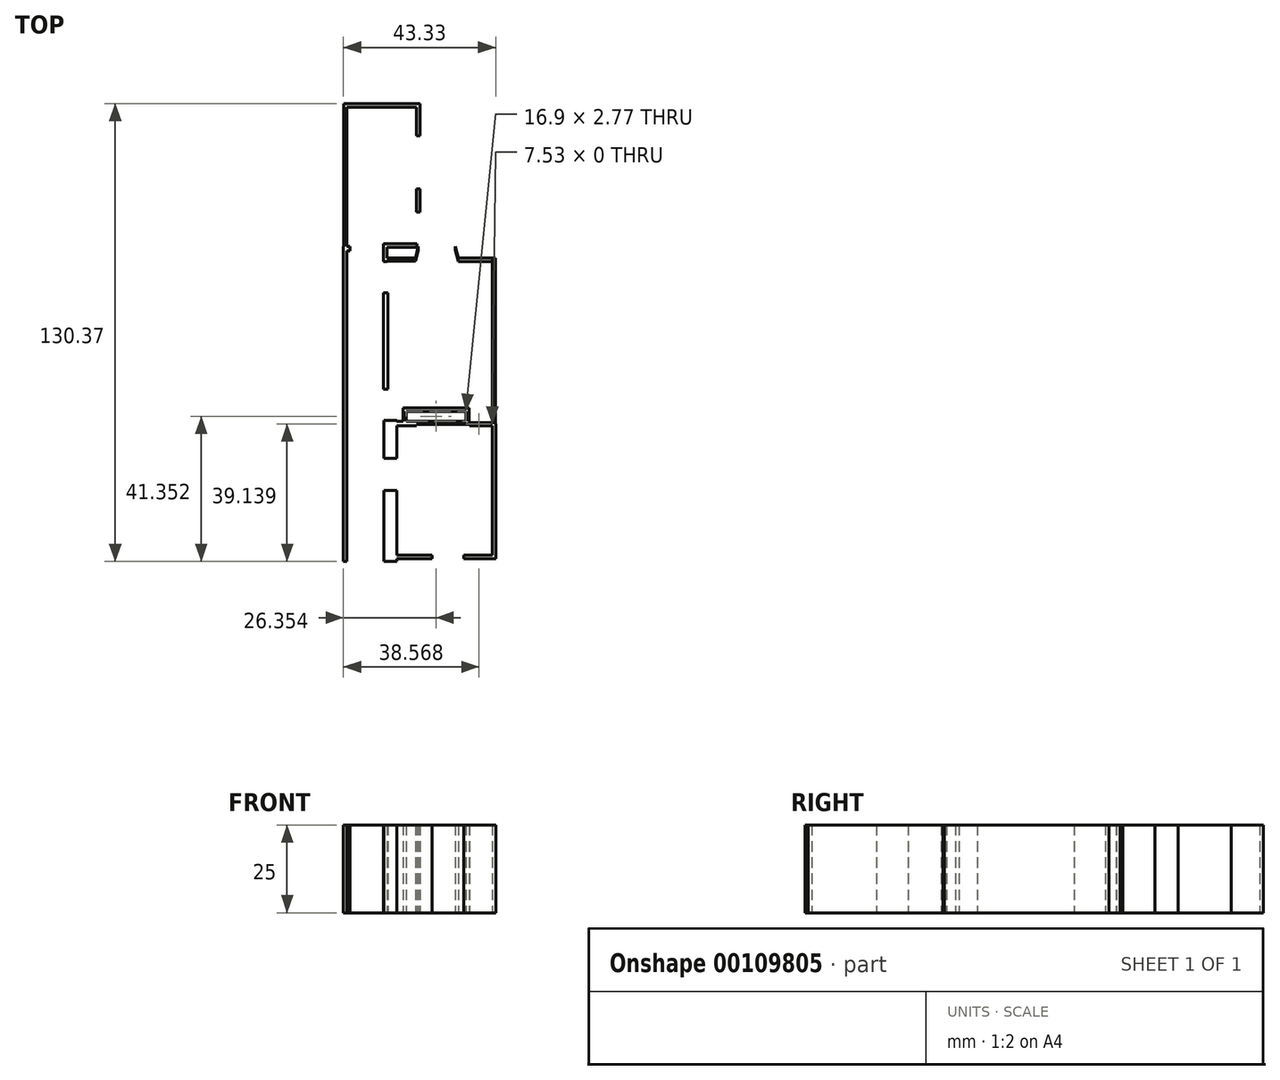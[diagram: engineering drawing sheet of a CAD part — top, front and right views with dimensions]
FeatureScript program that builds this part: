
annotation { "Feature Type Name" : "Feature", "Feature Type Description" : "" }
export const myFeature = defineFeature(function(context is Context, id is Id, definition is map)
    precondition{}
    {
        {
            var Q0;
            Q0=qCreatedBy(makeId("Top.planeOp"),FACE);
            var sketch = newSketch(context, id + "F0", { "sketchPlane" : qUnion([Q0])});
            skLineSegment(sketch, "E0.bottom", {"start": v(-26.92, 68.59) * mm, "end": v(-46.73, 68.59) * mm});
            skLineSegment(sketch, "E0.top", {"start": v(-26.92, 69.59) * mm, "end": v(-46.73, 69.59) * mm});
            skLineSegment(sketch, "E0.left", {"start": v(-26.92, 68.59) * mm, "end": v(-26.92, 69.59) * mm});
            skLineSegment(sketch, "E0.right", {"start": v(-46.73, 68.59) * mm, "end": v(-46.73, 69.59) * mm});
            skLineSegment(sketch, "E1.bottom", {"start": v(-26.94, 60.38) * mm, "end": v(-25.94, 60.38) * mm});
            skLineSegment(sketch, "E1.top", {"start": v(-26.94, 68.59) * mm, "end": v(-25.94, 68.59) * mm});
            skLineSegment(sketch, "E1.left", {"start": v(-26.94, 60.38) * mm, "end": v(-26.94, 68.59) * mm});
            skLineSegment(sketch, "E1.right", {"start": v(-25.94, 60.38) * mm, "end": v(-25.94, 68.59) * mm});
            skLineSegment(sketch, "E2.bottom", {"start": v(-46.74, 28.9) * mm, "end": v(-47.74, 28.9) * mm});
            skLineSegment(sketch, "E2.top", {"start": v(-46.74, 68.59) * mm, "end": v(-47.74, 68.59) * mm});
            skLineSegment(sketch, "E2.left", {"start": v(-46.74, 28.9) * mm, "end": v(-46.74, 68.59) * mm});
            skLineSegment(sketch, "E2.right", {"start": v(-47.74, 28.9) * mm, "end": v(-47.74, 68.59) * mm});
            skLineSegment(sketch, "E3.bottom", {"start": v(-46.74, 28.9) * mm, "end": v(-45.92, 28.9) * mm});
            skLineSegment(sketch, "E3.top", {"start": v(-46.74, 27.65) * mm, "end": v(-45.92, 27.65) * mm});
            skLineSegment(sketch, "E3.left", {"start": v(-46.74, 28.9) * mm, "end": v(-46.74, 27.65) * mm});
            skLineSegment(sketch, "E3.right", {"start": v(-45.92, 28.9) * mm, "end": v(-45.92, 27.65) * mm});
            skLineSegment(sketch, "E4.bottom", {"start": v(-36.42, 29.64) * mm, "end": v(-26.9, 29.64) * mm});
            skLineSegment(sketch, "E4.top", {"start": v(-36.42, 28.64) * mm, "end": v(-26.9, 28.64) * mm});
            skLineSegment(sketch, "E4.left", {"start": v(-36.42, 29.64) * mm, "end": v(-36.42, 28.64) * mm});
            skLineSegment(sketch, "E4.right", {"start": v(-26.9, 29.64) * mm, "end": v(-26.9, 28.64) * mm});
            skLineSegment(sketch, "E5.bottom", {"start": v(-36.42, 28.64) * mm, "end": v(-35.42, 28.64) * mm});
            skLineSegment(sketch, "E5.top", {"start": v(-36.42, 24.64) * mm, "end": v(-35.42, 24.64) * mm});
            skLineSegment(sketch, "E5.left", {"start": v(-36.42, 28.64) * mm, "end": v(-36.42, 24.64) * mm});
            skLineSegment(sketch, "E5.right", {"start": v(-35.42, 28.64) * mm, "end": v(-35.42, 24.64) * mm});
            skLineSegment(sketch, "E6.bottom", {"start": v(-27.25, 24.66) * mm, "end": v(-35.42, 24.66) * mm});
            skLineSegment(sketch, "E6.top", {"start": v(-27.25, 25.66) * mm, "end": v(-35.42, 25.66) * mm});
            skLineSegment(sketch, "E6.left", {"start": v(-27.25, 24.66) * mm, "end": v(-27.25, 25.66) * mm});
            skLineSegment(sketch, "E6.right", {"start": v(-35.42, 24.66) * mm, "end": v(-35.42, 25.66) * mm});
            skLineSegment(sketch, "E7.bottom", {"start": v(-26.49, 27.86) * mm, "end": v(-15.87, 27.86) * mm, "construction": true});
            skLineSegment(sketch, "E7.top", {"start": v(-26.49, 28.86) * mm, "end": v(-15.87, 28.86) * mm, "construction": true});
            skLineSegment(sketch, "E7.left", {"start": v(-26.49, 27.86) * mm, "end": v(-26.49, 28.86) * mm});
            skLineSegment(sketch, "E7.right", {"start": v(-15.87, 27.86) * mm, "end": v(-15.87, 28.86) * mm});
            skLineSegment(sketch, "E8", {"start": v(-26.49, 28.86) * mm, "end": v(-27.25, 25.66) * mm});
            skLineSegment(sketch, "E9", {"start": v(-27.25, 24.66) * mm, "end": v(-26.49, 27.86) * mm});
            skLineSegment(sketch, "E10.bottom", {"start": v(-5.45, 24.64) * mm, "end": v(-15.05, 24.64) * mm});
            skLineSegment(sketch, "E10.top", {"start": v(-5.45, 25.64) * mm, "end": v(-15.05, 25.64) * mm});
            skLineSegment(sketch, "E10.left", {"start": v(-5.45, 24.64) * mm, "end": v(-5.45, 25.64) * mm});
            skLineSegment(sketch, "E10.right", {"start": v(-15.05, 24.64) * mm, "end": v(-15.05, 25.64) * mm});
            skLineSegment(sketch, "E11", {"start": v(-15.87, 28.86) * mm, "end": v(-15.05, 25.64) * mm});
            skLineSegment(sketch, "E12", {"start": v(-15.87, 27.86) * mm, "end": v(-15.05, 24.64) * mm});
            skLineSegment(sketch, "E13.bottom", {"start": v(-5.44, -21.24) * mm, "end": v(-4.44, -21.24) * mm});
            skLineSegment(sketch, "E13.top", {"start": v(-5.44, 25.64) * mm, "end": v(-4.44, 25.64) * mm});
            skLineSegment(sketch, "E13.left", {"start": v(-5.44, -21.24) * mm, "end": v(-5.44, 25.64) * mm});
            skLineSegment(sketch, "E13.right", {"start": v(-4.44, -21.24) * mm, "end": v(-4.44, 25.64) * mm});
            skLineSegment(sketch, "E14.bottom", {"start": v(-36.34, 15.74) * mm, "end": v(-35.13, 15.74) * mm});
            skLineSegment(sketch, "E14.top", {"start": v(-36.34, -11.77) * mm, "end": v(-35.13, -11.77) * mm});
            skLineSegment(sketch, "E14.left", {"start": v(-36.34, 15.74) * mm, "end": v(-36.34, -11.77) * mm});
            skLineSegment(sketch, "E14.right", {"start": v(-35.13, 15.74) * mm, "end": v(-35.13, -11.77) * mm});
            skLineSegment(sketch, "E15.bottom", {"start": v(-26.92, 45.31) * mm, "end": v(-25.92, 45.31) * mm});
            skLineSegment(sketch, "E15.top", {"start": v(-26.92, 38.7) * mm, "end": v(-25.92, 38.7) * mm});
            skLineSegment(sketch, "E15.left", {"start": v(-26.92, 45.31) * mm, "end": v(-26.92, 38.7) * mm});
            skLineSegment(sketch, "E15.right", {"start": v(-25.92, 45.31) * mm, "end": v(-25.92, 38.7) * mm});
            skLineSegment(sketch, "E16.bottom", {"start": v(-46.74, 27.65) * mm, "end": v(-47.75, 27.65) * mm});
            skLineSegment(sketch, "E16.top", {"start": v(-46.74, -60.78) * mm, "end": v(-47.75, -60.78) * mm});
            skLineSegment(sketch, "E16.left", {"start": v(-46.74, 27.65) * mm, "end": v(-46.74, -60.78) * mm});
            skLineSegment(sketch, "E16.right", {"start": v(-47.75, 27.65) * mm, "end": v(-47.75, -60.78) * mm});
            skLineSegment(sketch, "E17.bottom", {"start": v(-30.85, -17.04) * mm, "end": v(-11.93, -17.04) * mm});
            skLineSegment(sketch, "E17.top", {"start": v(-30.85, -18.04) * mm, "end": v(-11.93, -18.04) * mm});
            skLineSegment(sketch, "E17.left", {"start": v(-30.85, -17.04) * mm, "end": v(-30.85, -18.04) * mm});
            skLineSegment(sketch, "E17.right", {"start": v(-11.93, -17.04) * mm, "end": v(-11.93, -18.04) * mm});
            skLineSegment(sketch, "E18.bottom", {"start": v(-30.85, -20.81) * mm, "end": v(-29.85, -20.81) * mm});
            skLineSegment(sketch, "E18.top", {"start": v(-30.85, -18.04) * mm, "end": v(-29.85, -18.04) * mm});
            skLineSegment(sketch, "E18.left", {"start": v(-30.85, -20.81) * mm, "end": v(-30.85, -18.04) * mm});
            skLineSegment(sketch, "E18.right", {"start": v(-29.85, -20.81) * mm, "end": v(-29.85, -18.04) * mm});
            skLineSegment(sketch, "E19.bottom", {"start": v(-11.94, -21.27) * mm, "end": v(-12.94, -21.27) * mm});
            skLineSegment(sketch, "E19.top", {"start": v(-11.94, -18.04) * mm, "end": v(-12.94, -18.04) * mm});
            skLineSegment(sketch, "E19.left", {"start": v(-11.94, -21.27) * mm, "end": v(-11.94, -18.04) * mm});
            skLineSegment(sketch, "E19.right", {"start": v(-12.94, -21.27) * mm, "end": v(-12.94, -18.04) * mm});
            skLineSegment(sketch, "E20.bottom", {"start": v(-12.94, -21.27) * mm, "end": v(-4.44, -21.27) * mm});
            skLineSegment(sketch, "E20.top", {"start": v(-12.94, -21.64) * mm, "end": v(-4.44, -21.64) * mm});
            skLineSegment(sketch, "E20.left", {"start": v(-12.94, -21.27) * mm, "end": v(-12.94, -21.64) * mm});
            skLineSegment(sketch, "E20.right", {"start": v(-4.44, -21.27) * mm, "end": v(-4.44, -21.64) * mm});
            skLineSegment(sketch, "E21.bottom", {"start": v(-36.27, -20.62) * mm, "end": v(-32.5, -20.62) * mm});
            skLineSegment(sketch, "E21.top", {"start": v(-36.27, -31.46) * mm, "end": v(-32.5, -31.46) * mm});
            skLineSegment(sketch, "E21.left", {"start": v(-36.27, -20.62) * mm, "end": v(-36.27, -31.46) * mm});
            skLineSegment(sketch, "E21.right", {"start": v(-32.5, -20.62) * mm, "end": v(-32.5, -31.46) * mm});
            skLineSegment(sketch, "E22.bottom", {"start": v(-27.02, -22.13) * mm, "end": v(-32.5, -22.13) * mm});
            skLineSegment(sketch, "E22.top", {"start": v(-27.02, -20.81) * mm, "end": v(-32.5, -20.81) * mm});
            skLineSegment(sketch, "E22.left", {"start": v(-27.02, -22.13) * mm, "end": v(-27.02, -20.81) * mm});
            skLineSegment(sketch, "E22.right", {"start": v(-32.5, -22.13) * mm, "end": v(-32.5, -20.81) * mm});
            skLineSegment(sketch, "E23.bottom", {"start": v(-11.82, -21.77) * mm, "end": v(-27.02, -21.77) * mm});
            skLineSegment(sketch, "E23.top", {"start": v(-11.82, -20.81) * mm, "end": v(-27.02, -20.81) * mm});
            skLineSegment(sketch, "E23.left", {"start": v(-11.82, -21.77) * mm, "end": v(-11.82, -20.81) * mm});
            skLineSegment(sketch, "E23.right", {"start": v(-27.02, -21.77) * mm, "end": v(-27.02, -20.81) * mm});
            skLineSegment(sketch, "E24.bottom", {"start": v(-5.42, -22.16) * mm, "end": v(-11.82, -22.16) * mm});
            skLineSegment(sketch, "E24.top", {"start": v(-5.42, -21.64) * mm, "end": v(-11.82, -21.64) * mm});
            skLineSegment(sketch, "E24.left", {"start": v(-5.42, -22.16) * mm, "end": v(-5.42, -21.64) * mm});
            skLineSegment(sketch, "E24.right", {"start": v(-11.82, -22.16) * mm, "end": v(-11.82, -21.64) * mm});
            skLineSegment(sketch, "E25.bottom", {"start": v(-5.42, -22.16) * mm, "end": v(-4.42, -22.16) * mm});
            skLineSegment(sketch, "E25.top", {"start": v(-5.42, -58.94) * mm, "end": v(-4.42, -58.94) * mm});
            skLineSegment(sketch, "E25.left", {"start": v(-5.42, -22.16) * mm, "end": v(-5.42, -58.94) * mm});
            skLineSegment(sketch, "E25.right", {"start": v(-4.42, -22.16) * mm, "end": v(-4.42, -58.94) * mm});
            skLineSegment(sketch, "E26.bottom", {"start": v(-4.42, -58.94) * mm, "end": v(-13.56, -58.94) * mm});
            skLineSegment(sketch, "E26.top", {"start": v(-4.42, -59.94) * mm, "end": v(-13.56, -59.94) * mm});
            skLineSegment(sketch, "E26.left", {"start": v(-4.42, -58.94) * mm, "end": v(-4.42, -59.94) * mm});
            skLineSegment(sketch, "E26.right", {"start": v(-13.56, -58.94) * mm, "end": v(-13.56, -59.94) * mm});
            skLineSegment(sketch, "E27.bottom", {"start": v(-22.53, -58.94) * mm, "end": v(-35.08, -58.94) * mm});
            skLineSegment(sketch, "E27.top", {"start": v(-22.53, -59.94) * mm, "end": v(-35.08, -59.94) * mm});
            skLineSegment(sketch, "E27.left", {"start": v(-22.53, -58.94) * mm, "end": v(-22.53, -59.94) * mm});
            skLineSegment(sketch, "E27.right", {"start": v(-35.08, -58.94) * mm, "end": v(-35.08, -59.94) * mm});
            skLineSegment(sketch, "E28.bottom", {"start": v(-32.53, -40.55) * mm, "end": v(-36.19, -40.55) * mm});
            skLineSegment(sketch, "E28.top", {"start": v(-32.53, -60.77) * mm, "end": v(-36.19, -60.77) * mm});
            skLineSegment(sketch, "E28.left", {"start": v(-32.53, -40.55) * mm, "end": v(-32.53, -60.77) * mm});
            skLineSegment(sketch, "E28.right", {"start": v(-36.19, -40.55) * mm, "end": v(-36.19, -60.77) * mm});
            skLineSegment(sketch, "E29.bottom", {"start": v(-46.73, 68.59) * mm, "end": v(-47.74, 68.59) * mm});
            skLineSegment(sketch, "E29.top", {"start": v(-46.73, 69.59) * mm, "end": v(-47.74, 69.59) * mm});
            skLineSegment(sketch, "E29.right", {"start": v(-47.74, 68.59) * mm, "end": v(-47.74, 69.59) * mm});
            skLineSegment(sketch, "E30.bottom", {"start": v(-26.92, 68.59) * mm, "end": v(-25.94, 68.59) * mm});
            skLineSegment(sketch, "E30.top", {"start": v(-26.92, 69.59) * mm, "end": v(-25.94, 69.59) * mm});
            skLineSegment(sketch, "E30.right", {"start": v(-25.94, 68.59) * mm, "end": v(-25.94, 69.59) * mm});
            skLineSegment(sketch, "E31.bottom", {"start": v(-46.74, 28.9) * mm, "end": v(-47.75, 28.9) * mm});
            skLineSegment(sketch, "E31.right", {"start": v(-47.75, 28.9) * mm, "end": v(-47.75, 27.65) * mm});
            skLineSegment(sketch, "E32.bottom", {"start": v(-4.42, -22.16) * mm, "end": v(-5.42, -22.16) * mm});
            skLineSegment(sketch, "E32.top", {"start": v(-4.42, -21.64) * mm, "end": v(-5.42, -21.64) * mm});
            skLineSegment(sketch, "E32.left", {"start": v(-4.42, -22.16) * mm, "end": v(-4.42, -21.64) * mm});
            skLineSegment(sketch, "E33", {"start": v(-29.85, -18.04) * mm, "end": v(-29.85, -20.81) * mm});
            skLineSegment(sketch, "E34", {"start": v(-27.02, -20.81) * mm, "end": v(-11.82, -20.81) * mm});
            skLineSegment(sketch, "E35", {"start": v(-12.94, -21.64) * mm, "end": v(-11.82, -21.64) * mm});
            skSolve(sketch);
        }
        {
            var Q0;
            Q0 = qSketchRegion(id + "F0", true);
            extrude(context, id + "F1", {"entities" : qUnion([Q0]), "depth" : 25 * mm});
        }
    });
